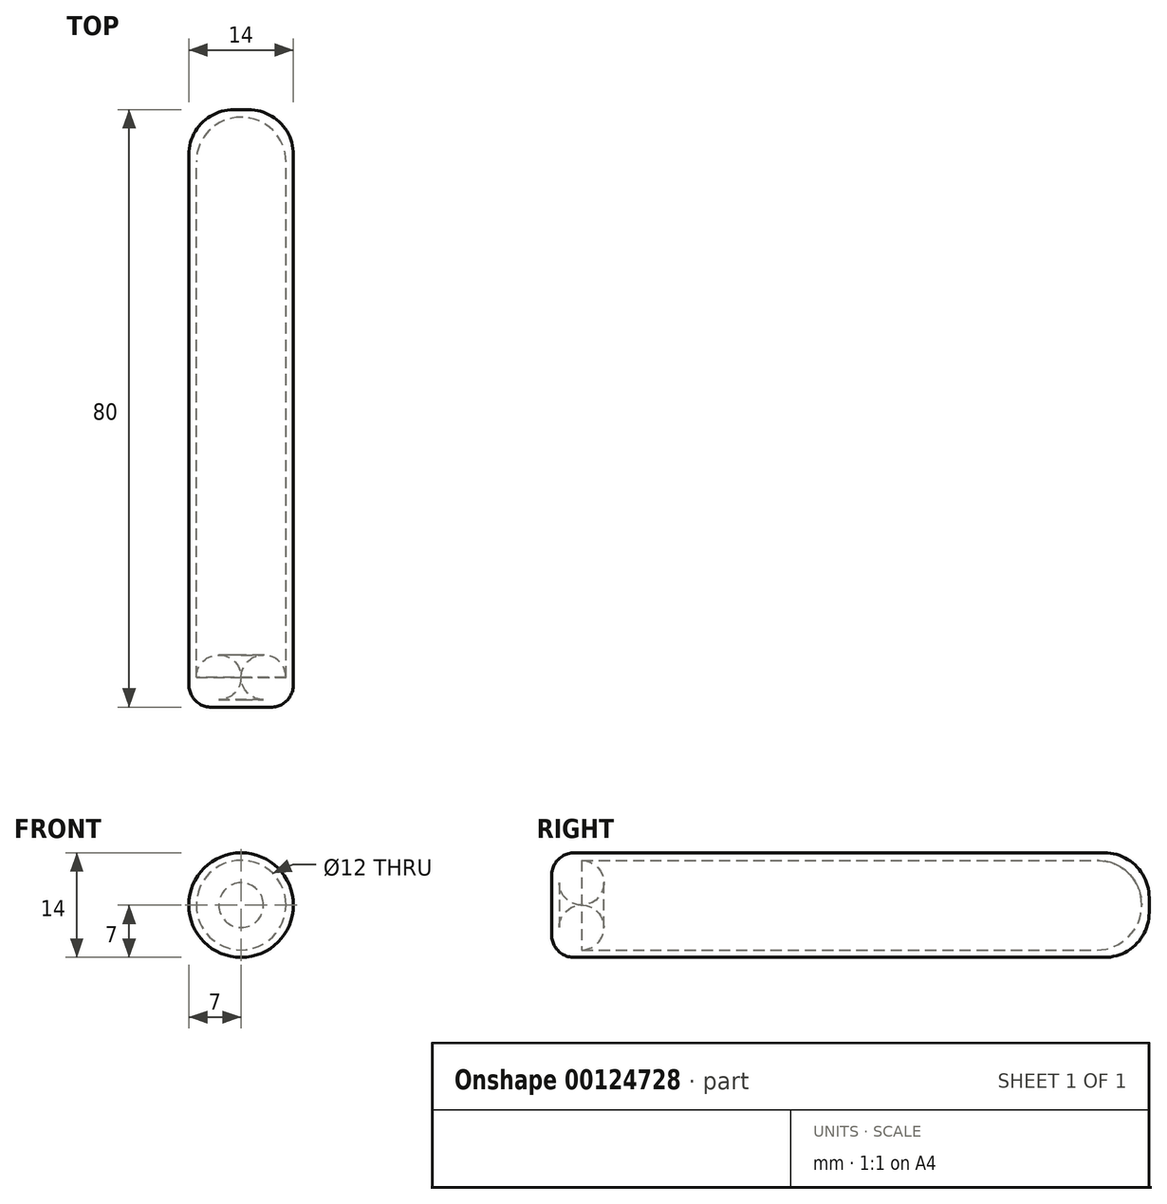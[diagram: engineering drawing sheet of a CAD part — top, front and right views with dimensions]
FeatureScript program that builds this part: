
annotation { "Feature Type Name" : "Feature", "Feature Type Description" : "" }
export const myFeature = defineFeature(function(context is Context, id is Id, definition is map)
    precondition{}
    {
        {
            var Q0;
            Q0=qCreatedBy(makeId("Right.planeOp"),FACE);
            var sketch = newSketch(context, id + "F0", { "sketchPlane" : qUnion([Q0])});
            skLineSegment(sketch, "E0.bottom", {"start": v(0, 0) * mm, "end": v(-80, 0) * mm, "construction": true});
            skLineSegment(sketch, "E0.top", {"start": v(-6, 7) * mm, "end": v(-77, 7) * mm});
            skLineSegment(sketch, "E0.left", {"start": v(0, 0) * mm, "end": v(0, 1) * mm});
            skLineSegment(sketch, "E0.right", {"start": v(-80, 0) * mm, "end": v(-80, 4) * mm});
            skLineSegment(sketch, "E1", {"start": v(-80, 0) * mm, "end": v(-79, 0) * mm});
            skLineSegment(sketch, "E2", {"start": v(-79, 0) * mm, "end": v(-79, 3) * mm});
            skLineSegment(sketch, "E3", {"start": v(-76, 6) * mm, "end": v(-7, 6) * mm});
            skLineSegment(sketch, "E4", {"start": v(-1, 0) * mm, "end": v(-1, 0) * mm});
            skLineSegment(sketch, "E5", {"start": v(-1, 0) * mm, "end": v(0, 0) * mm});
            skPoint(sketch, "E6.visualSharp", {"position": v(0, 7) * mm});
            skArc(sketch, "E6.filletArc", {"start": v(0, 1) * mm, "mid": v(-1.76, 5.24) * mm, "end": v(-6, 7) * mm});
            skPoint(sketch, "E7.visualSharp", {"position": v(-1, 6) * mm});
            skArc(sketch, "E7.filletArc", {"start": v(-1, 0) * mm, "mid": v(-2.76, 4.24) * mm, "end": v(-7, 6) * mm});
            skPoint(sketch, "E8.visualSharp", {"position": v(-80, 7) * mm});
            skArc(sketch, "E8.filletArc", {"start": v(-77, 7) * mm, "mid": v(-79.12, 6.12) * mm, "end": v(-80, 4) * mm});
            skPoint(sketch, "E9.visualSharp", {"position": v(-79, 6) * mm});
            skArc(sketch, "E9.filletArc", {"start": v(-76, 6) * mm, "mid": v(-78.12, 5.12) * mm, "end": v(-79, 3) * mm});
            skSolve(sketch);
        }
        {
            var Q0;
            Q0=makeQuery(id+"F0.imprint","IMPRINT",FACE,{"disambiguationData":[TD([[makeQuery(id+"F0.imprint","IMPRINT",EDGE,{"derivedFrom":sQuery(id+"F0.wireOp",EDGE,"E0.top")}),1.0]])]});
            var Q1;
            Q1=sQuery(id+"F0.wireOp",EDGE,"E0.bottom");
            revolve(context, id + "F1", {"entities" : qUnion([Q0]), "axis" : qUnion([Q1]), "revolveType" : RevolveType.FULL});
        }
    });
